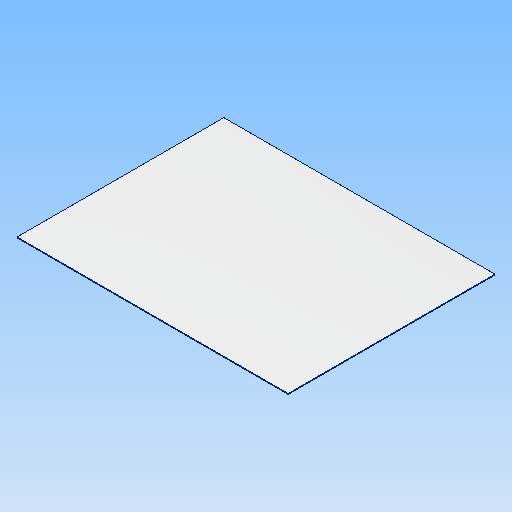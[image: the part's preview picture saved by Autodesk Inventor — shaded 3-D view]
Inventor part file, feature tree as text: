
AUTODESK INVENTOR PART (.ipt)
format: ipt  version: 2021 (Build 250183000, 183)  size: 84,480 bytes
history: native  units: in
note: dims shown in document units (in); Inventor stores cm internally (conversion verified against a paired STEP export)
features: extrude x1, sketch x1
ambient origin geometry x8: Origin, YZ Plane, XZ Plane, XY Plane, X Axis, Y Axis, Z Axis, Center Point
bodies: Solid1 (feature_tree)
feature tree (2):
  extrude  "Extrusion1"  [1 undecoded]
  sketch  "Sketch1"  dims[d2=0.063in d3=0.0in]
note: 1 required parameter value undecoded (feature->parameter linkage not recoverable at this tier; creation-order binding heuristic only, values carry confidence <= 0.55)
